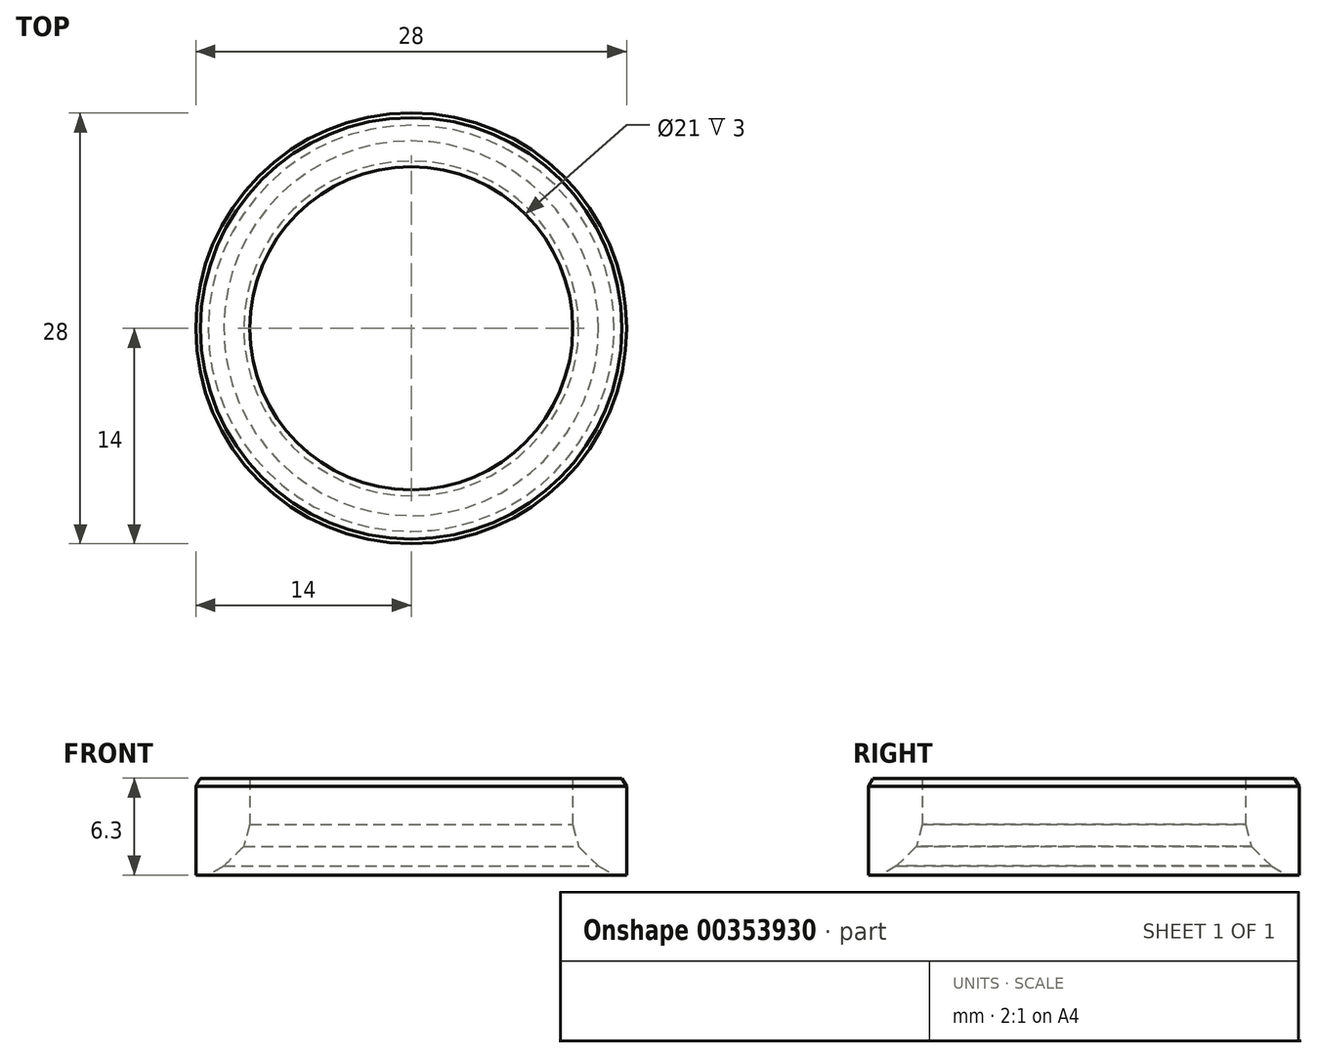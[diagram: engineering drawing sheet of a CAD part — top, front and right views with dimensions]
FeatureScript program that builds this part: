
annotation { "Feature Type Name" : "Feature", "Feature Type Description" : "" }
export const myFeature = defineFeature(function(context is Context, id is Id, definition is map)
    precondition{}
    {
        {
            var Q0;
            Q0=qCreatedBy(makeId("Front.planeOp"),FACE);
            var sketch = newSketch(context, id + "F0", { "sketchPlane" : qUnion([Q0])});
            skLineSegment(sketch, "E0", {"start": v(0, -5.16) * mm, "end": v(0, 98.57) * mm, "construction": true});
            skLineSegment(sketch, "E1", {"start": v(12.3, 1.3) * mm, "end": v(10.77, 2.8) * mm});
            skLineSegment(sketch, "E2", {"start": v(10.77, 2.8) * mm, "end": v(7.86, 4.5) * mm});
            skLineSegment(sketch, "E3", {"start": v(12.3, 1.3) * mm, "end": v(12.3, 0.3) * mm});
            skLineSegment(sketch, "E4", {"start": v(12.3, 0.3) * mm, "end": v(12, 0) * mm});
            skLineSegment(sketch, "E5", {"start": v(12, 0) * mm, "end": v(0, 0) * mm});
            skLineSegment(sketch, "E6", {"start": v(0, 98.57) * mm, "end": v(0, 0) * mm});
            skArc(sketch, "E7", {"start": v(2.94, 12.6) * mm, "mid": v(4.38, 7.94) * mm, "end": v(7.86, 4.5) * mm});
            skLineSegment(sketch, "E8", {"start": v(10.5, 7.13) * mm, "end": v(10.5, 4.13) * mm});
            skLineSegment(sketch, "E9", {"start": v(10.5, 4.13) * mm, "end": v(10.88, 2.7) * mm});
            skLineSegment(sketch, "E10", {"start": v(10.88, 2.7) * mm, "end": v(12.18, 1.41) * mm});
            skLineSegment(sketch, "E11", {"start": v(13.2, 0.83) * mm, "end": v(12.18, 1.41) * mm});
            skLineSegment(sketch, "E12", {"start": v(13.7, 7.13) * mm, "end": v(10.5, 7.13) * mm});
            skLineSegment(sketch, "E13", {"start": v(13.2, 0.83) * mm, "end": v(14, 0.83) * mm});
            skLineSegment(sketch, "E14", {"start": v(14, 0.83) * mm, "end": v(14, 6.6) * mm});
            skLineSegment(sketch, "E15", {"start": v(14, 6.6) * mm, "end": v(13.7, 7.13) * mm});
            skLineSegment(sketch, "E16", {"start": v(2.94, 12.6) * mm, "end": v(2.7, 17.27) * mm});
            skLineSegment(sketch, "E17", {"start": v(2.5, 19.61) * mm, "end": v(2.5, 98.57) * mm});
            skArc(sketch, "E18", {"start": v(2.5, 19.61) * mm, "mid": v(2.55, 18.44) * mm, "end": v(2.7, 17.27) * mm});
            skLineSegment(sketch, "E19", {"start": v(2.5, 98.57) * mm, "end": v(0, 98.57) * mm});
            skSolve(sketch);
        }
        {
            var Q0;
            Q0=makeQuery(id+"F0.imprint","IMPRINT",FACE,{"disambiguationData":[TD([[makeQuery(id+"F0.imprint","IMPRINT",EDGE,{"derivedFrom":sQuery(id+"F0.wireOp",EDGE,"E8")}),1.0]])]});
            var Q1;
            Q1=sQuery(id+"F0.wireOp",EDGE,"E0");
            revolve(context, id + "F1", {"surfaceOperationType" : NewSurfaceOperationType.NEW, "entities" : qUnion([Q0]), "axis" : qUnion([Q1]), "revolveType" : RevolveType.FULL});
        }
    });
